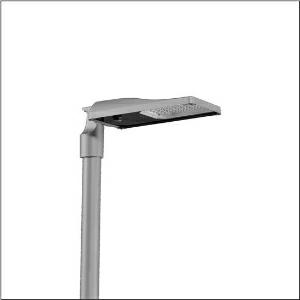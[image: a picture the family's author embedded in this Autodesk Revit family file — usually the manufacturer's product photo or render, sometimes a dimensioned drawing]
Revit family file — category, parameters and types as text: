
# Revit family: streetlight_sl_31_mini___st1_0a_5xh2d31r08ja_e878
name_source: partatom
category: Lighting Fixtures
units: mm (PartAtom-declared; Revit-internal decimal feet)

## family parameters
Cut with Voids When Loaded = No
Host = Face
Light Source = No
Part Type = Normal
Room Calculation Point = No
Round Connector Dimension = Use Diameter
Shared = No

## types (1)
- --- (1 x LED, 12270 lm, 82.5 W, 3000K)
    Apparent Load = 83 VA
    CIE Flux Codes = 40 73 97 100 100
    Color Rendering = 70
    Color Temperature = 3000K
    Default Elevation = 1800 mm
    Description = Streetlight SL 31 mini D4i, Desk-Remote mast luminaire for post-top, side-entry; light control with lens of PMMA; light distribution: ST1.0a, direct asymmetric distribution, for standard-compliant lighting for roads and squares; LED: luminous flux: 12.270lm, light colour: 730, colour temperature: 3000K; luminous efficacy: 148,7lm/W; control: pre-setting: logarithmic dimming characteristic, flexible luminous flux parameterisation, time-dependent luminous flux control, constant luminous flux control, power reduction, intelligent temperature release in ECG and LED module, overheat protection; luminaire housing, of diecast aluminium, SITECO metallic grey (DB 702S), corrosivity category C5 high according to DIN EN ISO 12944; cover of toughened safety glass, transparent, mast flange of diecast aluminium, SITECO metallic grey (DB 702S), spigot size: 76/60mm, mast flange included unmounted; with cable H07RN-F 2x 1.5mm², cable length: 10,5m, connection cable pre-assembled; mains connection: 220..240V, AC, 50/60Hz; power consumption (at start of service life): 82,5W / (at end of service life): 90,1W / (with reduced operation 50%): 36,8W; protection rating (complete): IP66; insulation class (complete): insulation class II (safety insulation); impact resistance: IK09; certification: CE, ENEC, ENEC+, VDE, UKCA, ZD4i; permissible operating ambient temperature for outdoor applications: -40..+50°C; packaging unit: 1 piece

Light Distribution: ST1.0a
    Height = 76 mm
    Lamp = 1 x LED
    Lamp Light Flux = 12270 lm
    Lamp Power = 82.5 W
    Lamp count = 1
    Length = 547 mm
    Luminous efficacy = 149 lm/W
    Manufacturer = Siteco
    ModVariant = No
    Model = 5XH2D31R08JA
    Number of Poles = 1
    OnlyDefault = Yes
    Power Factor = 1
    Product Name = Streetlight SL 31 mini | ST1.0a
    Product group = mast luminaire | pylon top
    ProductGroupID = 6100
    Protection Class = Protection class II
    Protection Degree = IP 66
    RLX_Detail_Level = 1
    RLX_Emergency_Light_Flux = 0 lm
    RLX_Emergency_Type = 0
    RLX_Emergency_Type_DB = No
    RlxData = <blob elided: 39729 chars, md5=faee2686>
    Socket = socket
    Standby Power = 0 W
    System Light Flux = 12270 lm
    System Power = 83 W
    Type Comments = factory setting: luminous flux: 100 % | dim-lin: 254 | 870 mA
    Type Image = l_1300328.jpg
    URL = http://relux.com
    VarID = @adj_057795
    Voltage = 0 V
    Weight = 0.00 kg
    Width = 265 mm

## geometry (parser evidence)
native form markers: Blend x4, Sweep x8
no freeform markers — native parametric forms only
